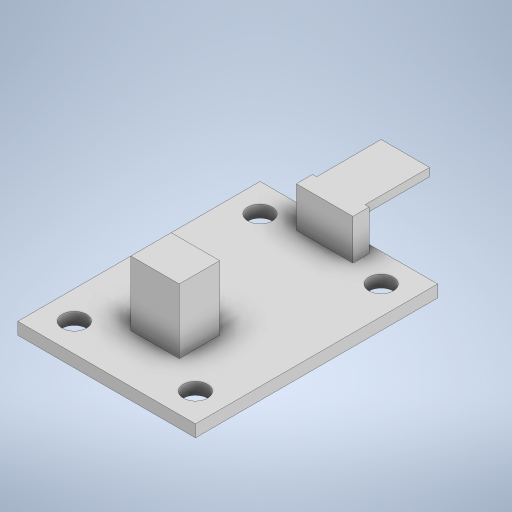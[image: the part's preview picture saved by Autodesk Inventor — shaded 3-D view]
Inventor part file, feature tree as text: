
AUTODESK INVENTOR PART (.ipt)
format: ipt  version: 2024 (Build 280153000, 153)  size: 285,696 bytes
history: native  units: mm
features: extrude x4, sketch x4, projected_geometry x1
ambient origin geometry x8: Origin, YZ Plane, XZ Plane, XY Plane, X Axis, Y Axis, Z Axis, Center Point
bodies: Solid1 (feature_tree)
feature tree (9):
  extrude  "Extrusion1"  Depth=22.0mm
  extrude  "Extrusion2"  Depth=1.5mm TaperAngle=0.0deg
  extrude  "Extrusion3"  Depth=2.0mm
  extrude  "Extrusion4"  Depth=5.0mm
  sketch  "Sketch1"  dims[d0=30.0mm d1=22.0mm]
  sketch  "Sketch2"  dims[d3=3.0mm d12=1.5mm d13=0.0mm]
  sketch  "Sketch3"  dims[d14=7.0mm d15=2.0mm]
  sketch  "Sketch4"  dims[d16=1.0mm d20=5.0mm d21=6.0mm d22=6.0mm d23=8.0mm d24=0.0mm d25=4.0mm d26=6.0mm d27=1.0mm d28=0.5mm d29=0.5mm d30=8.0mm d31=0.0mm d32=8.0mm d33=0.0mm d34=15.0mm d35=23.0mm d36=23.0mm d37=15.0mm]
  projected_geometry  "Projected Loop1"
